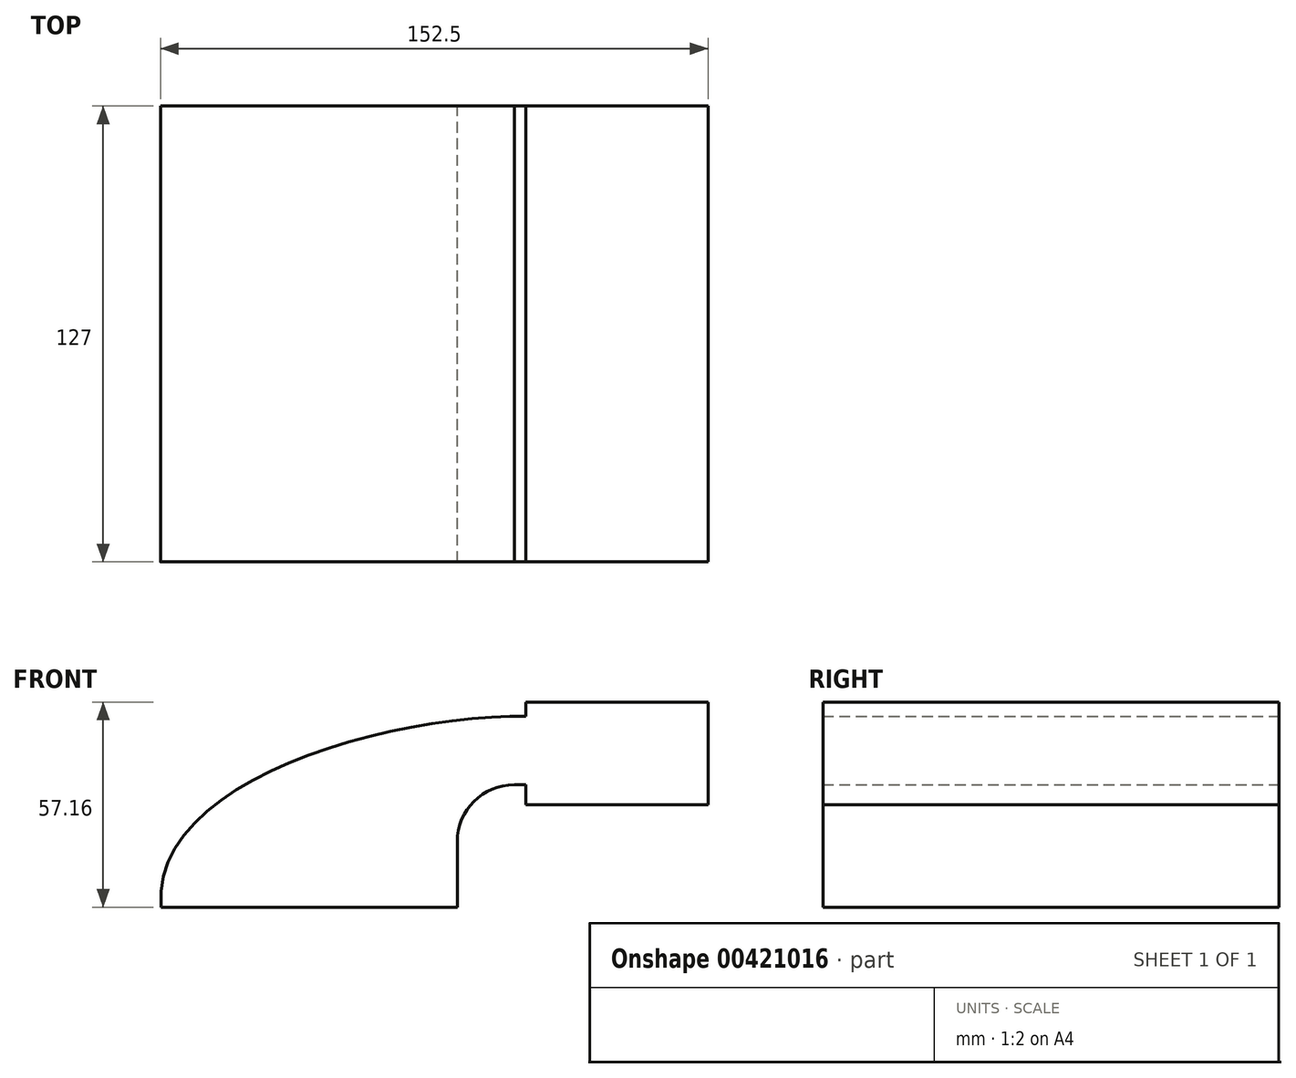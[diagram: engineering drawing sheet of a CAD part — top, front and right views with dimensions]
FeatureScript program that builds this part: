
annotation { "Feature Type Name" : "Feature", "Feature Type Description" : "" }
export const myFeature = defineFeature(function(context is Context, id is Id, definition is map)
    precondition{}
    {
        {
            var Q0;
            Q0=qCreatedBy(makeId("Front.planeOp"),FACE);
            var sketch = newSketch(context, id + "F0", { "sketchPlane" : qUnion([Q0])});
            skLineSegment(sketch, "E0.bottom", {"start": v(-41.28, 9.52) * mm, "end": v(41.27, 9.53) * mm});
            skLineSegment(sketch, "E0.top", {"start": v(-41.28, -9.53) * mm, "end": v(41.28, -9.53) * mm});
            skLineSegment(sketch, "E0.left", {"start": v(-41.28, 9.52) * mm, "end": v(-41.27, -9.53) * mm});
            skLineSegment(sketch, "E0.right", {"start": v(41.28, 9.53) * mm, "end": v(41.28, -9.52) * mm});
            skPoint(sketch, "E0.middle", {"position": v(0, 0) * mm});
            skLineSegment(sketch, "E1", {"start": v(41.27, 9.53) * mm, "end": v(41.27, 27.75) * mm});
            skArc(sketch, "E2", {"start": v(41.27, 27.75) * mm, "mid": v(45.92, 38.98) * mm, "end": v(57.15, 43.63) * mm});
            skLineSegment(sketch, "E3.bottom", {"start": v(60.33, 38.1) * mm, "end": v(111.13, 38.1) * mm});
            skLineSegment(sketch, "E3.top", {"start": v(60.33, 66.67) * mm, "end": v(111.13, 66.67) * mm});
            skLineSegment(sketch, "E3.left", {"start": v(60.33, 38.1) * mm, "end": v(60.33, 66.67) * mm});
            skLineSegment(sketch, "E3.right", {"start": v(111.13, 38.1) * mm, "end": v(111.13, 66.67) * mm});
            skPoint(sketch, "E3.middle", {"position": v(85.73, 52.39) * mm});
            skLineSegment(sketch, "E4", {"start": v(57.15, 43.63) * mm, "end": v(85.72, 43.63) * mm});
            skLineSegment(sketch, "E5.0", {"start": v(57.15, 62.68) * mm, "end": v(85.72, 62.68) * mm});
            skArc(sketch, "E5.1", {"start": v(22.22, 27.75) * mm, "mid": v(32.45, 52.45) * mm, "end": v(57.15, 62.68) * mm});
            skLineSegment(sketch, "E5.2", {"start": v(22.23, 9.53) * mm, "end": v(22.23, 27.75) * mm});
            skLineSegment(sketch, "E6", {"start": v(85.73, 38.1) * mm, "end": v(85.73, 66.67) * mm});
            skFitSpline(sketch, "E7", {"points": [v(-41.28, 9.52) * mm, v(57.15, 62.68) * mm], "startDerivative": vector(-8.71, 103.69) * mm, "endDerivative": vector(114.53, 1.49) * mm});
            skSolve(sketch);
        }
        {
            var Q0;
            {var subQ0=sQuery(id+"F0.wireOp",EDGE,"E7");var subQ1=sQuery(id+"F0.wireOp",EDGE,"E5.1");var subQ3=makeQuery(id+"F0.imprint","INTERSECT",VERTEX,{"derivedFrom":[subQ1,subQ0]});Q0=makeQuery(id+"F0.imprint","IMPRINT",FACE,{"disambiguationData":[TD([[makeQuery(id+"F0.imprint","IMPRINT",EDGE,{"disambiguationData":[TD([[subQ3,-1.0]])],"derivedFrom":subQ1}),-1.0]])]});}
            var Q1;
            {var subQ3=sQuery(id+"F0.wireOp",EDGE,"E5.2");Q1=makeQuery(id+"F0.imprint","IMPRINT",FACE,{"disambiguationData":[TD([[makeQuery(id+"F0.imprint","IMPRINT",EDGE,{"derivedFrom":subQ3}),1.0]])]});}
            var Q2;
            {var subQ0=sQuery(id+"F0.wireOp",EDGE,"E3.left");var subQ1=sQuery(id+"F0.wireOp",EDGE,"E3.bottom");var subQ2=makeQuery(id+"F0.imprint","INTERSECT",VERTEX,{"derivedFrom":[subQ1,subQ0]});Q2=makeQuery(id+"F0.imprint","IMPRINT",FACE,{"disambiguationData":[TD([[makeQuery(id+"F0.imprint","IMPRINT",EDGE,{"disambiguationData":[TD([[subQ2,-1.0]])],"derivedFrom":subQ1}),1.0]])]});}
            var Q3;
            {var subQ0=sQuery(id+"F0.wireOp",EDGE,"E3.left");var subQ1=sQuery(id+"F0.wireOp",EDGE,"E3.top");var subQ2=makeQuery(id+"F0.imprint","INTERSECT",VERTEX,{"derivedFrom":[subQ1,subQ0]});Q3=makeQuery(id+"F0.imprint","IMPRINT",FACE,{"disambiguationData":[TD([[makeQuery(id+"F0.imprint","IMPRINT",EDGE,{"disambiguationData":[TD([[subQ2,-1.0]])],"derivedFrom":subQ1}),-1.0]])]});}
            var Q4;
            {var subQ4=sQuery(id+"F0.wireOp",EDGE,"E3.right");Q4=makeQuery(id+"F0.imprint","IMPRINT",FACE,{"disambiguationData":[TD([[makeQuery(id+"F0.imprint","IMPRINT",EDGE,{"derivedFrom":subQ4}),1.0]])]});}
            var Q5;
            {var subQ5=sQuery(id+"F0.wireOp",EDGE,"E1");Q5=makeQuery(id+"F0.imprint","IMPRINT",FACE,{"disambiguationData":[TD([[makeQuery(id+"F0.imprint","IMPRINT",EDGE,{"derivedFrom":subQ5}),1.0]])]});}
            var Q6;
            {var subQ0=sQuery(id+"F0.wireOp",EDGE,"E4");var subQ1=sQuery(id+"F0.wireOp",EDGE,"E3.left");var subQ2=makeQuery(id+"F0.imprint","INTERSECT",VERTEX,{"derivedFrom":[subQ1,subQ0]});Q6=makeQuery(id+"F0.imprint","IMPRINT",FACE,{"disambiguationData":[TD([[makeQuery(id+"F0.imprint","IMPRINT",EDGE,{"disambiguationData":[TD([[subQ2,-1.0]])],"derivedFrom":subQ1}),-1.0]])]});}
            extrude(context, id + "F1", {"entities" : qUnion([Q0, Q1, Q2, Q3, Q4, Q5, Q6]), "endBound" : BoundingType.SYMMETRIC, "depth" : 127 * mm});
        }
    });
